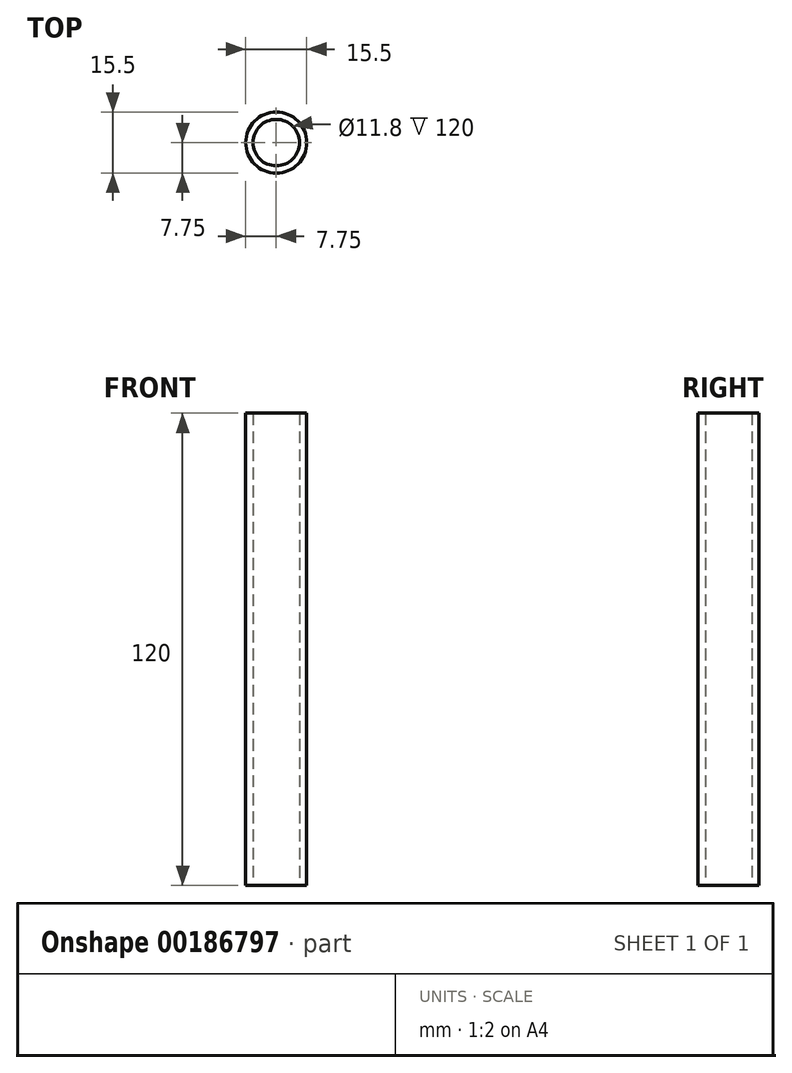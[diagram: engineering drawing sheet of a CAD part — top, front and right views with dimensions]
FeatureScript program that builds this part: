
annotation { "Feature Type Name" : "Feature", "Feature Type Description" : "" }
export const myFeature = defineFeature(function(context is Context, id is Id, definition is map)
    precondition{}
    {
        {
            var Q0;
            Q0=qCreatedBy(makeId("Top.planeOp"),FACE);
            var sketch = newSketch(context, id + "F0", { "sketchPlane" : qUnion([Q0])});
            skCircle(sketch, "E0", {"center": v(0, 0) * mm, "radius": 7.75 * mm});
            skCircle(sketch, "E1", {"center": v(0, 0) * mm, "radius": 5.9 * mm});
            skSolve(sketch);
        }
        {
            var Q0;
            Q0=makeQuery(id+"F0.imprint","IMPRINT",FACE,{"disambiguationData":[TD([[makeQuery(id+"F0.imprint","IMPRINT",EDGE,{"derivedFrom":sQuery(id+"F0.wireOp",EDGE,"k1lLN6mw-iSQl-95vs-SuBk-9JJAK6DFVB2c.bottom")}),-1.0]])]});
            var Q1;
            Q1=makeQuery(id+"F0.imprint","IMPRINT",FACE,{"disambiguationData":[TD([[makeQuery(id+"F0.imprint","IMPRINT",EDGE,{"derivedFrom":sQuery(id+"F0.wireOp",EDGE,"E0")}),1.0]])]});
            extrude(context, id + "F1", {"entities" : qUnion([Q0, Q1]), "depth" : 120 * mm});
        }
    });
